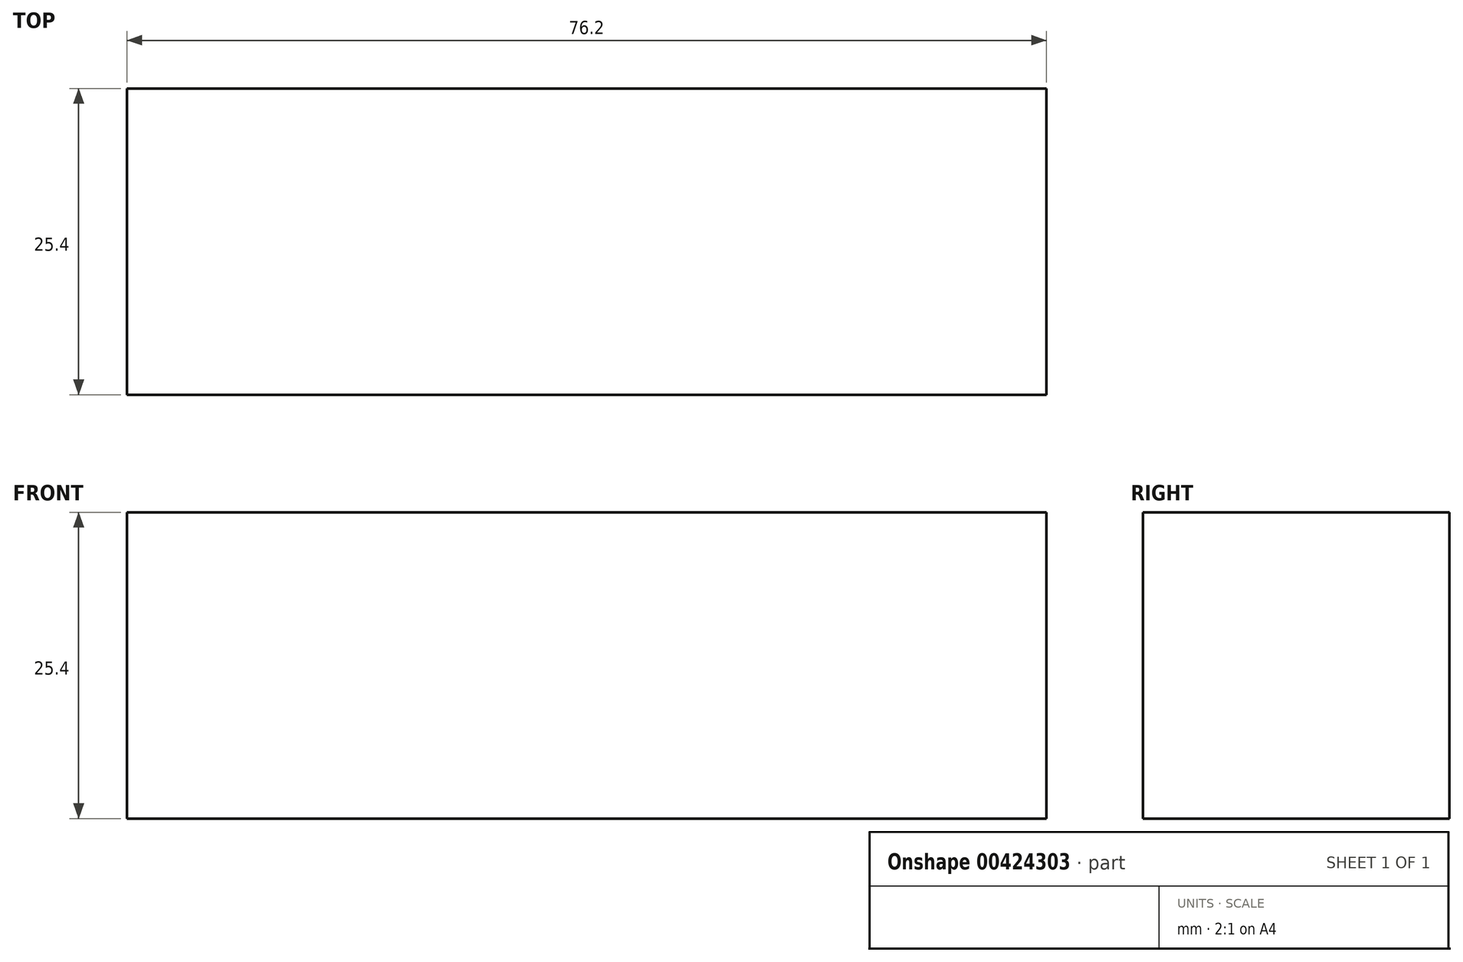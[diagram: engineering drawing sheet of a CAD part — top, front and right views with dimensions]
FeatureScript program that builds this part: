
annotation { "Feature Type Name" : "Feature", "Feature Type Description" : "" }
export const myFeature = defineFeature(function(context is Context, id is Id, definition is map)
    precondition{}
    {
        {
            var Q0;
            Q0=qCreatedBy(makeId("Front.planeOp"),FACE);
            var sketch = newSketch(context, id + "F0", { "sketchPlane" : qUnion([Q0])});
            skLineSegment(sketch, "E0.bottom", {"start": v(0, 0) * mm, "end": v(-76.2, 0) * mm});
            skLineSegment(sketch, "E0.top", {"start": v(0, 25.4) * mm, "end": v(-76.2, 25.4) * mm});
            skLineSegment(sketch, "E0.left", {"start": v(0, 0) * mm, "end": v(0, 25.4) * mm});
            skLineSegment(sketch, "E0.right", {"start": v(-76.2, 0) * mm, "end": v(-76.2, 25.4) * mm});
            skLineSegment(sketch, "E1.bottom", {"start": v(-76.2, 25.4) * mm, "end": v(-50.8, 25.4) * mm});
            skLineSegment(sketch, "E1.top", {"start": v(-76.2, 50.8) * mm, "end": v(-50.8, 50.8) * mm});
            skLineSegment(sketch, "E1.left", {"start": v(-76.2, 25.4) * mm, "end": v(-76.2, 50.8) * mm});
            skLineSegment(sketch, "E1.right", {"start": v(-50.8, 25.4) * mm, "end": v(-50.8, 50.8) * mm});
            skSolve(sketch);
        }
        {
            var Q0;
            Q0=makeQuery(id+"F0.imprint","IMPRINT",FACE,{"disambiguationData":[TD([[makeQuery(id+"F0.imprint","IMPRINT",EDGE,{"derivedFrom":sQuery(id+"F0.wireOp",EDGE,"E0.bottom")}),-1.0]])]});
            var Q1;
            Q1=makeQuery(id+"F0.imprint","IMPRINT",FACE,{"disambiguationData":[TD([[makeQuery(id+"F0.imprint","IMPRINT",EDGE,{"derivedFrom":sQuery(id+"F0.wireOp",EDGE,"E1.bottom")}),1.0]])]});
            extrude(context, id + "F1", {"entities" : qUnion([Q0, Q1]), "depth" : 25.4 * mm});
        }
    });
